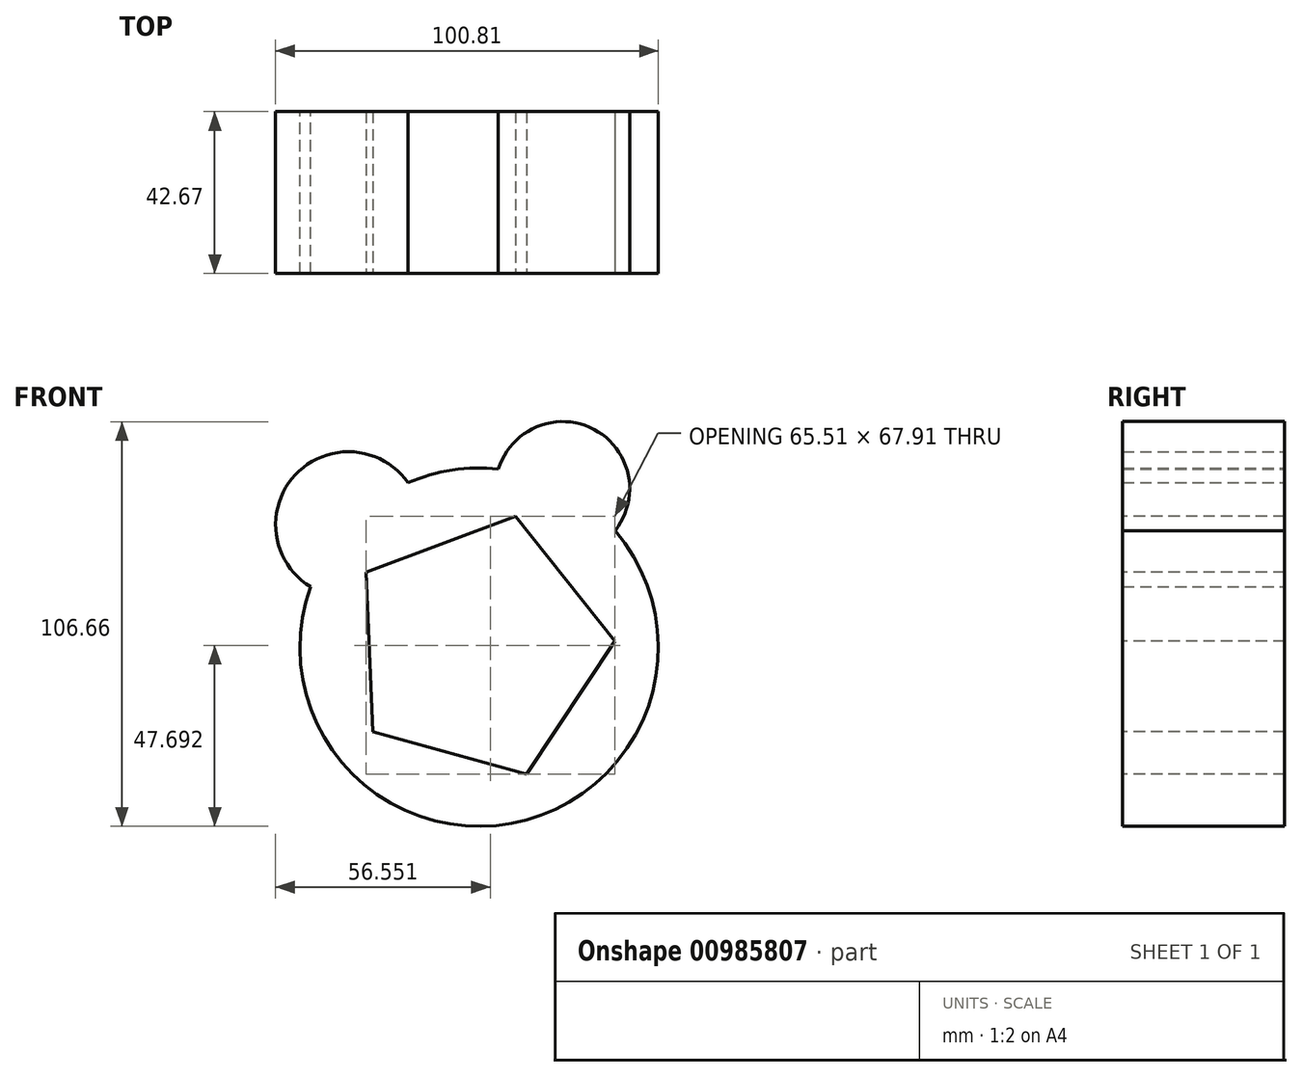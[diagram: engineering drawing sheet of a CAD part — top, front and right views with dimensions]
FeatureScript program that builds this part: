
annotation { "Feature Type Name" : "Feature", "Feature Type Description" : "" }
export const myFeature = defineFeature(function(context is Context, id is Id, definition is map)
    precondition{}
    {
        {
            var Q0;
            Q0=qCreatedBy(makeId("Front.planeOp"),FACE);
            var sketch = newSketch(context, id + "F0", { "sketchPlane" : qUnion([Q0])});
            skCircle(sketch, "E0", {"center": v(0, 0) * mm, "radius": 47.2 * mm});
            skCircle(sketch, "E1", {"center": v(22, 41.77) * mm, "radius": 17.69 * mm});
            skCircle(sketch, "E2", {"center": v(-34.41, 32.31) * mm, "radius": 19.2 * mm});
            skCircle(sketch, "E3", {"center": v(-44.57, 47.63) * mm, "radius": 5.92 * mm});
            skSolve(sketch);
        }
        {
            var Q0;
            {var subQ0=sQuery(id+"F0.wireOp",EDGE,"E2");var subQ1=sQuery(id+"F0.wireOp",EDGE,"E0");var subQ2=makeQuery(id+"F0.imprint","INTERSECT",VERTEX,{"disambiguationData":[OD(0.0)],"derivedFrom":[subQ1,subQ0]});Q0=makeQuery(id+"F0.imprint","IMPRINT",FACE,{"disambiguationData":[TD([[makeQuery(id+"F0.imprint","IMPRINT",EDGE,{"disambiguationData":[TD([[subQ2,-1.0]])],"derivedFrom":subQ1}),-1.0]])]});}
            var Q1;
            {var subQ0=sQuery(id+"F0.wireOp",EDGE,"E2");var subQ1=sQuery(id+"F0.wireOp",EDGE,"E0");var subQ2=makeQuery(id+"F0.imprint","INTERSECT",VERTEX,{"disambiguationData":[OD(0.0)],"derivedFrom":[subQ1,subQ0]});Q1=makeQuery(id+"F0.imprint","IMPRINT",FACE,{"disambiguationData":[TD([[makeQuery(id+"F0.imprint","IMPRINT",EDGE,{"disambiguationData":[TD([[subQ2,-1.0]])],"derivedFrom":subQ1}),1.0]])]});}
            var Q2;
            {var subQ0=sQuery(id+"F0.wireOp",EDGE,"E1");var subQ1=sQuery(id+"F0.wireOp",EDGE,"E0");var subQ2=makeQuery(id+"F0.imprint","INTERSECT",VERTEX,{"disambiguationData":[OD(0.0)],"derivedFrom":[subQ1,subQ0]});Q2=makeQuery(id+"F0.imprint","IMPRINT",FACE,{"disambiguationData":[TD([[makeQuery(id+"F0.imprint","IMPRINT",EDGE,{"disambiguationData":[TD([[subQ2,1.0]])],"derivedFrom":subQ1}),-1.0]])]});}
            var Q3;
            {var subQ0=sQuery(id+"F0.wireOp",EDGE,"E1");var subQ1=sQuery(id+"F0.wireOp",EDGE,"E0");var subQ2=makeQuery(id+"F0.imprint","INTERSECT",VERTEX,{"disambiguationData":[OD(0.0)],"derivedFrom":[subQ1,subQ0]});Q3=makeQuery(id+"F0.imprint","IMPRINT",FACE,{"disambiguationData":[TD([[makeQuery(id+"F0.imprint","IMPRINT",EDGE,{"disambiguationData":[TD([[subQ2,-1.0]])],"derivedFrom":subQ1}),1.0]])]});}
            var Q4;
            {var subQ0=sQuery(id+"F0.wireOp",EDGE,"E1");var subQ1=sQuery(id+"F0.wireOp",EDGE,"E0");var subQ2=makeQuery(id+"F0.imprint","INTERSECT",VERTEX,{"disambiguationData":[OD(0.0)],"derivedFrom":[subQ1,subQ0]});Q4=makeQuery(id+"F0.imprint","IMPRINT",FACE,{"disambiguationData":[TD([[makeQuery(id+"F0.imprint","IMPRINT",EDGE,{"disambiguationData":[TD([[subQ2,1.0]])],"derivedFrom":subQ1}),1.0]])]});}
            var Q5;
            {var subQ0=sQuery(id+"F0.wireOp",EDGE,"E3");var subQ1=sQuery(id+"F0.wireOp",EDGE,"E2");var subQ2=makeQuery(id+"F0.imprint","INTERSECT",VERTEX,{"disambiguationData":[OD(0.0)],"derivedFrom":[subQ1,subQ0]});Q5=makeQuery(id+"F0.imprint","IMPRINT",FACE,{"disambiguationData":[TD([[makeQuery(id+"F0.imprint","IMPRINT",EDGE,{"disambiguationData":[TD([[subQ2,-1.0]])],"derivedFrom":subQ1}),1.0]])]});}
            extrude(context, id + "F1", {"entities" : qUnion([Q0, Q1, Q2, Q3, Q4, Q5]), "depth" : 42.67 * mm, "offsetDistance" : 25.4 * mm});
        }
        {
            var Q0;
            Q0=makeQuery(id+"F1.opExtrude","CAP_FACE",FACE,{"disambiguationData":[OSD([sQuery(id+"F0.wireOp",EDGE,"E0"),sQuery(id+"F0.wireOp",EDGE,"E1"),sQuery(id+"F0.wireOp",EDGE,"E2")])],"isStart":false});
            var sketch = newSketch(context, id + "F2", { "sketchPlane" : qUnion([Q0])});
            skCircle(sketch, "E4.cCircle", {"center": v(0, 0) * mm, "radius": 28.91 * mm, "construction": true});
            skLineSegment(sketch, "E4.0", {"start": v(9.55, 34.44) * mm, "end": v(35.7, 1.56) * mm});
            skLineSegment(sketch, "E4.1", {"start": v(35.7, 1.56) * mm, "end": v(12.52, -33.48) * mm});
            skLineSegment(sketch, "E4.2", {"start": v(12.52, -33.48) * mm, "end": v(-27.97, -22.25) * mm});
            skLineSegment(sketch, "E4.3", {"start": v(-27.97, -22.25) * mm, "end": v(-29.8, 19.73) * mm});
            skLineSegment(sketch, "E4.4", {"start": v(-29.8, 19.73) * mm, "end": v(9.55, 34.44) * mm});
            skPoint(sketch, "E4.0.midPoint", {"position": v(22.63, 18) * mm});
            skSolve(sketch);
        }
        {
            var Q0;
            Q0=makeQuery(id+"F2.imprint","IMPRINT",FACE,{"disambiguationData":[TD([[makeQuery(id+"F2.imprint","IMPRINT",EDGE,{"derivedFrom":sQuery(id+"F2.wireOp",EDGE,"E4.0")}),-1.0]])]});
            extrude(context, id + "F3", {"entities" : qUnion([Q0]), "operationType" : NewBodyOperationType.REMOVE, "oppositeDirection" : true, "depth" : 175.5 * mm, "offsetDistance" : 25.4 * mm});
        }
    });
